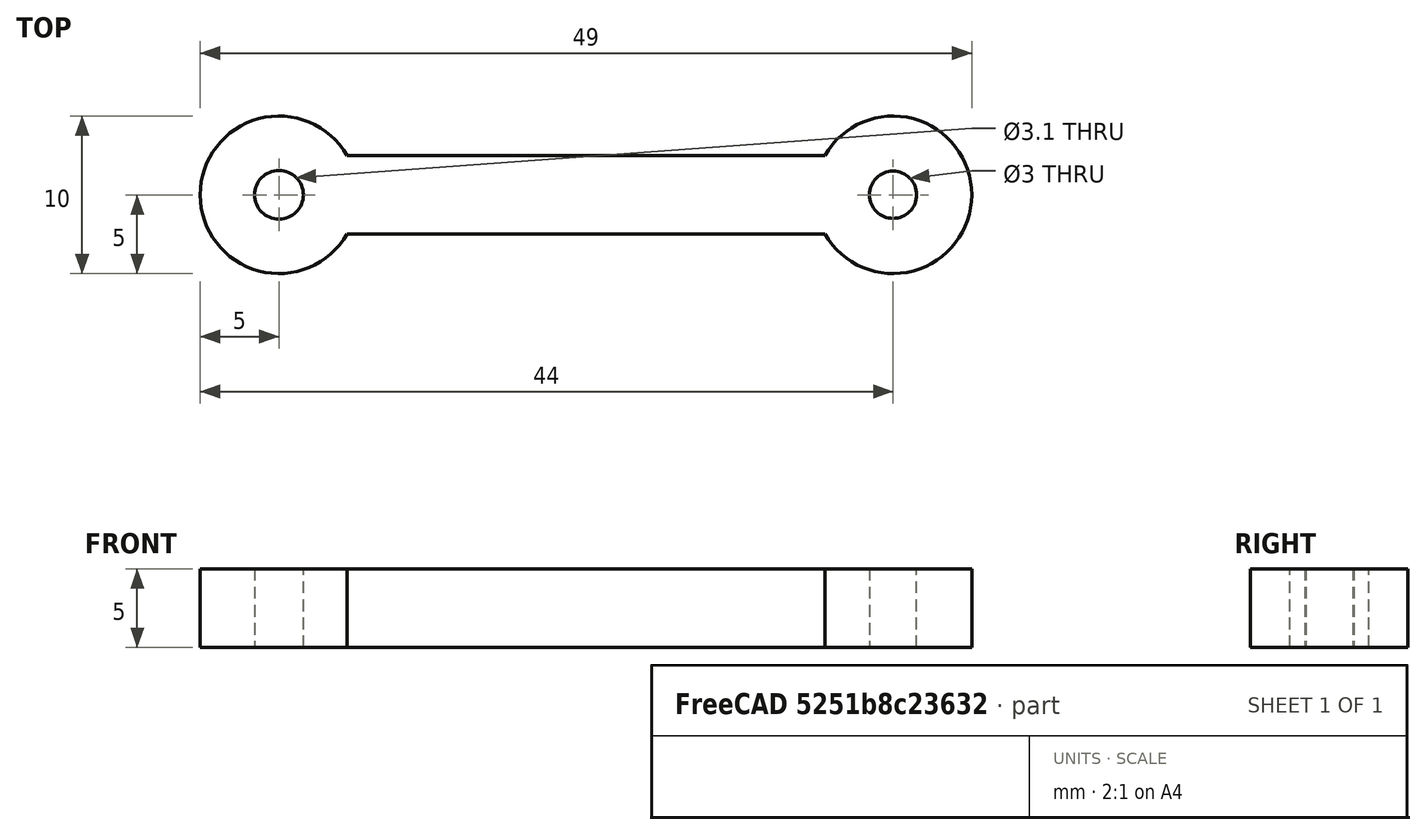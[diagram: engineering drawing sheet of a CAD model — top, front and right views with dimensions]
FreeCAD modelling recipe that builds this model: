
FCSTD DOCUMENT  (FreeCAD 0.14R3702 (Git))
Label: plaquita-pinza-v2
License: CC-BY 3.0
LicenseURL: http://creativecommons.org/licenses/by/3.0/
objects: Sketcher::SketchObject×1, Part::Extrusion×1
note: 2 computed .brp shape members not serialized (recipe doc carries the construction recipe); baked Part::Feature solids carry a one-line shape summary decoded from their .brp

FEATURE [Sketcher::SketchObject] Sketch  label="sk-main"
  sketch-geometry (6):
    g0: ArcOfCircle CenterX=-19.5 CenterY=0 CenterZ=0 NormalX=0 NormalY=0 NormalZ=1 Radius=5 StartAngle=0.523599 EndAngle=5.75959
    g1: Circle CenterX=-19.5 CenterY=0 CenterZ=0 NormalX=0 NormalY=0 NormalZ=1 Radius=1.55
    g2: LineSegment StartX=-15.1699 StartY=2.5 StartZ=0 EndX=15.1699 EndY=2.5 EndZ=0
    g3: LineSegment StartX=15.1699 StartY=-2.5 StartZ=0 EndX=-15.1699 EndY=-2.5 EndZ=0
    g4: ArcOfCircle CenterX=19.5 CenterY=0 CenterZ=0 NormalX=0 NormalY=0 NormalZ=1 Radius=5 StartAngle=3.66519 EndAngle=8.90118
    g5: Circle CenterX=19.5 CenterY=0 CenterZ=0 NormalX=0 NormalY=0 NormalZ=1 Radius=1.5
  constraints (16):
    c: Radius(g1) = 1.55
    c: Coincident(g0,g3)
    c: Horizontal(g2)
    c: Horizontal(g3)
    c: Radius(g0) = 5
    c: Coincident(g0,g2)
    c: Symmetric(g2,g0,g-2)
    c: Coincident(g0,g1)
    c: Coincident(g4,g5)
    c: Coincident(g2,g4)
    c: Coincident(g3,g4)
    c: Radius(g5) = 1.5
    c: DistanceX(g0,g4) = 39
    c: Symmetric(g4,g0,g-2)
    c: Symmetric(g3,g2,g-1)
    c: DistanceY(g2,g3) = -5
FEATURE [Part::Extrusion] Extrude  label="cuerpo"
  Base = -> Sketch
  Dir = (0,0,5)
  Solid = true
